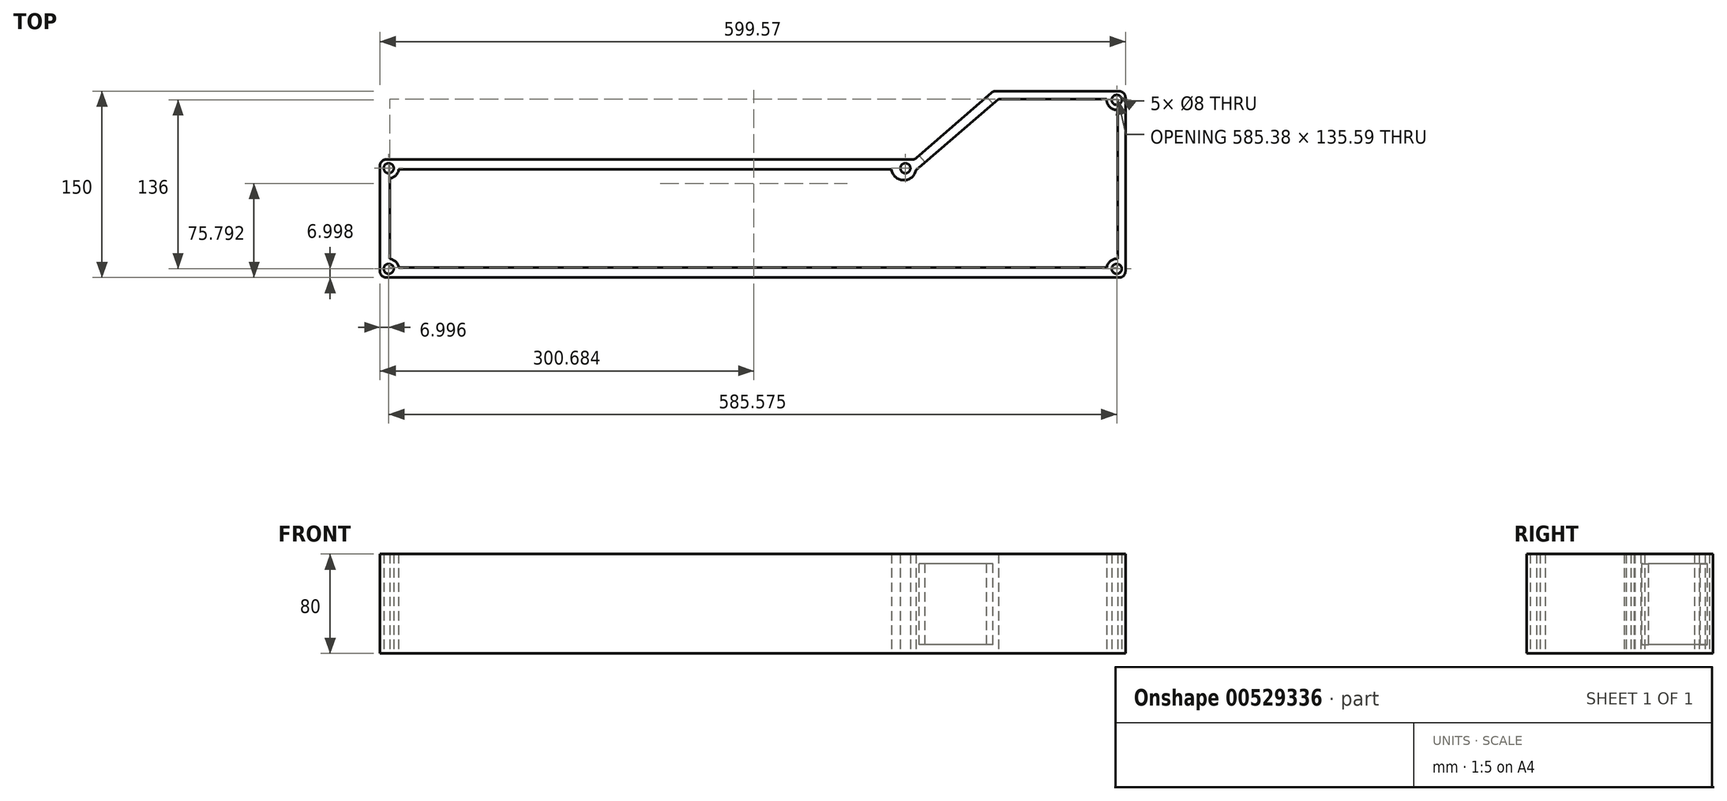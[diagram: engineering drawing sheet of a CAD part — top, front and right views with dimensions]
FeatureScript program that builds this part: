
annotation { "Feature Type Name" : "Feature", "Feature Type Description" : "" }
export const myFeature = defineFeature(function(context is Context, id is Id, definition is map)
    precondition{}
    {
        {
            var Q0;
            Q0=qCreatedBy(makeId("Top.planeOp"),FACE);
            var sketch = newSketch(context, id + "F0", { "sketchPlane" : qUnion([Q0])});
            skLineSegment(sketch, "E0.bottom", {"start": v(213.5, 75.9) * mm, "end": v(313, 75.9) * mm});
            skLineSegment(sketch, "E0.top", {"start": v(-276.58, -74.1) * mm, "end": v(313, -74.1) * mm});
            skLineSegment(sketch, "E0.left", {"start": v(-281.58, 15.9) * mm, "end": v(-281.58, -69.1) * mm});
            skLineSegment(sketch, "E0.right", {"start": v(318, 70.9) * mm, "end": v(318, -69.1) * mm});
            skLineSegment(sketch, "E1", {"start": v(210.22, 74.68) * mm, "end": v(149.83, 22.14) * mm});
            skLineSegment(sketch, "E2", {"start": v(146.55, 20.9) * mm, "end": v(-276.58, 20.9) * mm});
            skCircle(sketch, "E3", {"center": v(-274.58, 13.9) * mm, "radius": 4 * mm});
            skCircle(sketch, "E4", {"center": v(-274.58, -67.1) * mm, "radius": 4 * mm});
            skCircle(sketch, "E5", {"center": v(311, -67.1) * mm, "radius": 4 * mm});
            skCircle(sketch, "E6", {"center": v(311, 68.9) * mm, "radius": 4 * mm});
            skCircle(sketch, "E7", {"center": v(141, 13.9) * mm, "radius": 4 * mm});
            skPoint(sketch, "E8.visualSharp", {"position": v(-281.58, -74.1) * mm});
            skArc(sketch, "E8.filletArc", {"start": v(-281.58, -69.1) * mm, "mid": v(-280.12, -72.63) * mm, "end": v(-276.58, -74.1) * mm});
            skPoint(sketch, "E9.newPointB", {"position": v(-281.58, 20.9) * mm});
            skArc(sketch, "E9.filletArc", {"start": v(-276.58, 20.9) * mm, "mid": v(-280.12, 19.44) * mm, "end": v(-281.58, 15.9) * mm});
            skPoint(sketch, "E10.newPointB", {"position": v(-282, 75.9) * mm});
            skArc(sketch, "E10.filletArc", {"start": v(213.5, 75.9) * mm, "mid": v(211.75, 75.6) * mm, "end": v(210.22, 74.68) * mm});
            skPoint(sketch, "E11.visualSharp", {"position": v(148.42, 20.9) * mm});
            skArc(sketch, "E11.filletArc", {"start": v(146.55, 20.9) * mm, "mid": v(148.3, 21.23) * mm, "end": v(149.83, 22.14) * mm});
            skPoint(sketch, "E12.visualSharp", {"position": v(318, 75.9) * mm});
            skArc(sketch, "E12.filletArc", {"start": v(318, 70.9) * mm, "mid": v(316.53, 74.44) * mm, "end": v(313, 75.9) * mm});
            skPoint(sketch, "E13.visualSharp", {"position": v(318, -74.1) * mm});
            skArc(sketch, "E13.filletArc", {"start": v(313, -74.1) * mm, "mid": v(316.53, -72.63) * mm, "end": v(318, -69.1) * mm});
            skLineSegment(sketch, "E14", {"start": v(-273.58, 5.9) * mm, "end": v(-273.58, -59.1) * mm});
            skLineSegment(sketch, "E15", {"start": v(-266.58, 12.9) * mm, "end": v(-112.41, 12.9) * mm});
            skArc(sketch, "E16", {"start": v(-273.58, 5.9) * mm, "mid": v(-268.87, 8.2) * mm, "end": v(-266.58, 12.9) * mm});
            skLineSegment(sketch, "E17", {"start": v(-266.58, -66.1) * mm, "end": v(303, -66.1) * mm});
            skArc(sketch, "E18", {"start": v(-266.58, -66.1) * mm, "mid": v(-268.87, -61.38) * mm, "end": v(-273.58, -59.1) * mm});
            skLineSegment(sketch, "E19", {"start": v(311.8, 60.9) * mm, "end": v(311.8, -59.1) * mm});
            skLineSegment(sketch, "E20", {"start": v(303, 69.5) * mm, "end": v(221.92, 69.5) * mm});
            skArc(sketch, "E21", {"start": v(311.8, -59.1) * mm, "mid": v(305.95, -60.78) * mm, "end": v(303, -66.1) * mm});
            skArc(sketch, "E22", {"start": v(303, 69.5) * mm, "mid": v(305.38, 63.14) * mm, "end": v(311.8, 60.9) * mm});
            skLineSegment(sketch, "E23", {"start": v(-112.41, 12.9) * mm, "end": v(129.8, 12.9) * mm});
            skLineSegment(sketch, "E24", {"start": v(221.92, 69.5) * mm, "end": v(215.82, 69.5) * mm});
            skLineSegment(sketch, "E25", {"start": v(215.82, 69.5) * mm, "end": v(149.5, 12.37) * mm});
            skArc(sketch, "E26", {"start": v(129.8, 12.9) * mm, "mid": v(139.42, 4.3) * mm, "end": v(149.5, 12.37) * mm});
            skSolve(sketch);
        }
        {
            var Q0;
            Q0=makeQuery(id+"F0.imprint","IMPRINT",FACE,{"disambiguationData":[TD([[makeQuery(id+"F0.imprint","IMPRINT",EDGE,{"derivedFrom":sQuery(id+"F0.wireOp",EDGE,"E0.bottom")}),-1.0]])]});
            extrude(context, id + "F1", {"entities" : qUnion([Q0]), "depth" : 80 * mm, "offsetDistance" : 25 * mm});
        }
        {
            var Q0;
            Q0=makeQuery(id+"F1.opExtrude","SWEPT_FACE",FACE,{"disambiguationData":[OSD([sQuery(id+"F0.wireOp",EDGE,"E1")])]});
            var sketch = newSketch(context, id + "F2", { "sketchPlane" : qUnion([Q0])});
            skLineSegment(sketch, "E27.bottom", {"start": v(-202.6, 7.17) * mm, "end": v(-130.6, 7.17) * mm});
            skLineSegment(sketch, "E27.top", {"start": v(-202.6, 72.17) * mm, "end": v(-130.6, 72.17) * mm});
            skLineSegment(sketch, "E27.left", {"start": v(-202.6, 7.17) * mm, "end": v(-202.6, 72.17) * mm});
            skLineSegment(sketch, "E27.right", {"start": v(-130.6, 7.17) * mm, "end": v(-130.6, 72.17) * mm});
            skSolve(sketch);
        }
        {
            var Q0;
            Q0=makeQuery(id+"F2.imprint","IMPRINT",FACE,{"disambiguationData":[TD([[makeQuery(id+"F2.imprint","IMPRINT",EDGE,{"derivedFrom":sQuery(id+"F2.wireOp",EDGE,"E27.bottom")}),1.0]])]});
            extrude(context, id + "F3", {"entities" : qUnion([Q0]), "operationType" : NewBodyOperationType.REMOVE, "endBound" : BoundingType.UP_TO_NEXT, "oppositeDirection" : true, "depth" : 7.2 * mm, "offsetDistance" : 25 * mm});
        }
    });
